# Revit family: RV 4212 01 Eslim 60x60 Empotrable Armstrong 40W
name_source: partatom
category: Luminarias
revit_build: Autodesk Revit 2015 (Build: 20140606_1530(x64)
units: mm (PartAtom-declared; Revit-internal decimal feet)

## types (2) — shared parameters
Anchura rectángulo de emisión = 566 mm  [stored 1.85696 ft]
Cambio de temperatura de color de luz atenuada = <Ninguno>
Fabricante = SECOM ILUMINACIÓN
Filtro de color = 16777215
Forma visible en renderización = No
Longitud de rectángulo de emisión = 566 mm  [stored 1.85696 ft]
Lámpara = LED Osram Duris E3 Plus
Modelo = ESLIM DE EMPOTRAR 60X60
Ángulo de inclinación = 90.00°

## per-type parameters (varying)
| type | Archivo de red fotométrica | Comentarios de vataje | Descripción |
| Eslim 60x60 de empotrar en techo registrable o Armstrong de 40W | 4212 01 84.IES | 40 W | 4212 01 84 |
| Eslim 60x60 de empotrar en techo Armstrong de 60W | 4112 01 60 84.IES | 60W | 4112 01 60 84 |

note: [stored X ft] marks values corroborated as IEEE doubles in the binary element streams (Revit-internal decimal feet)
